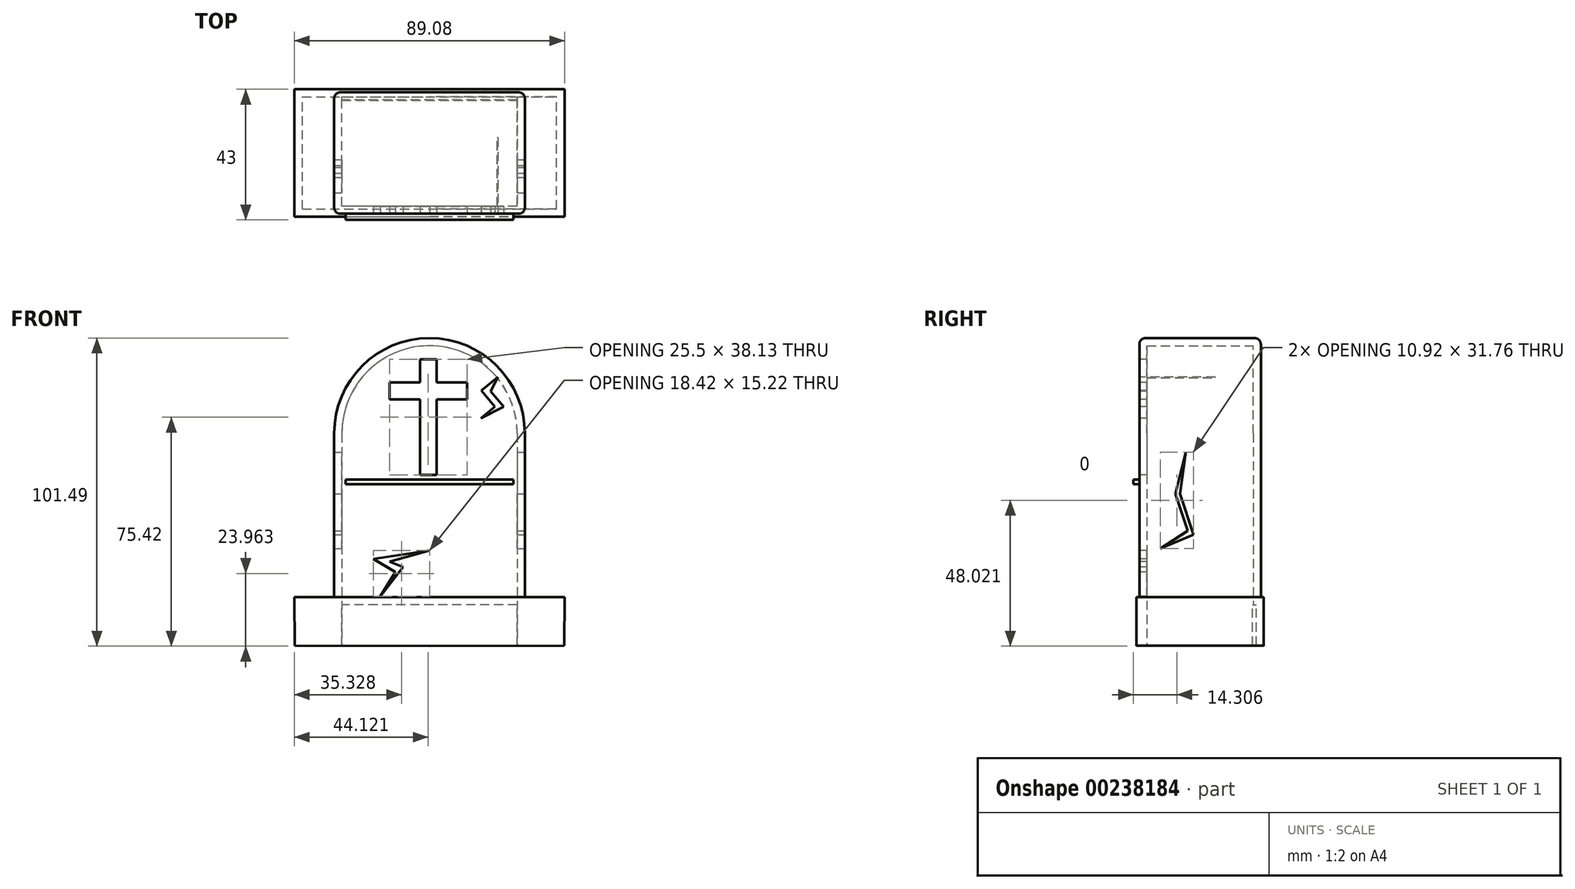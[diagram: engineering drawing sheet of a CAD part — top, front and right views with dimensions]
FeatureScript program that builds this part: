
annotation { "Feature Type Name" : "Feature", "Feature Type Description" : "" }
export const myFeature = defineFeature(function(context is Context, id is Id, definition is map)
    precondition{}
    {
        {
            var Q0;
            Q0=qCreatedBy(makeId("Front.planeOp"),FACE);
            var sketch = newSketch(context, id + "F0", { "sketchPlane" : qUnion([Q0])});
            skLineSegment(sketch, "E0", {"start": v(31.39, 27.06) * mm, "end": v(31.39, -27.25) * mm});
            skLineSegment(sketch, "E1.MirrorCS", {"start": v(-31.39, 27.06) * mm, "end": v(-31.39, -27.25) * mm});
            skArc(sketch, "E2", {"start": v(31.39, 27.06) * mm, "mid": v(0, 58.45) * mm, "end": v(-31.39, 27.06) * mm});
            skLineSegment(sketch, "E3", {"start": v(-31.39, -27.25) * mm, "end": v(31.39, -27.25) * mm});
            skSolve(sketch);
        }
        {
            var Q0;
            Q0 = qSketchRegion(id + "F0", true);
            extrude(context, id + "F1", {"entities" : qUnion([Q0]), "endBound" : BoundingType.SYMMETRIC, "depth" : 40 * mm});
        }
        {
            var Q0;
            Q0=qCreatedBy(makeId("Front.planeOp"),FACE);
            var sketch = newSketch(context, id + "F2", { "sketchPlane" : qUnion([Q0])});
            skLineSegment(sketch, "E4", {"start": v(-31.2, -26.88) * mm, "end": v(-44.54, -26.88) * mm});
            skLineSegment(sketch, "E5", {"start": v(-44.54, -26.88) * mm, "end": v(-44.4, -42.88) * mm});
            skLineSegment(sketch, "E6", {"start": v(-44.4, -42.88) * mm, "end": v(0.02, -43.04) * mm});
            skLineSegment(sketch, "E7.MirrorCS", {"start": v(44.54, -26.88) * mm, "end": v(44.4, -42.88) * mm});
            skLineSegment(sketch, "E8.MirrorCS", {"start": v(31.2, -26.88) * mm, "end": v(44.54, -26.88) * mm});
            skLineSegment(sketch, "E9.MirrorCS", {"start": v(44.4, -42.88) * mm, "end": v(-0.02, -43.04) * mm});
            skLineSegment(sketch, "E10", {"start": v(-31.2, -26.88) * mm, "end": v(31.2, -26.88) * mm});
            skSolve(sketch);
        }
        {
            var Q0;
            Q0 = qSketchRegion(id + "F2", true);
            extrude(context, id + "F3", {"entities" : qUnion([Q0]), "operationType" : NewBodyOperationType.ADD, "endBound" : BoundingType.SYMMETRIC, "depth" : 42 * mm});
        }
        {
            var Q0;
            Q0=makeQuery(id+"F3.opExtrude","SWEPT_FACE",FACE,{"disambiguationData":[OSD([sQuery(id+"F2.wireOp",EDGE,"E6")])]});
            var Q1;
            Q1=makeQuery(id+"F3.opExtrude","SWEPT_FACE",FACE,{"disambiguationData":[OSD([sQuery(id+"F2.wireOp",EDGE,"E9.MirrorCS")])]});
            shell(context, id + "F4", {"entities" : qUnion([Q0, Q1]), "thickness" : 2.5 * mm});
        }
        {
            var Q0;
            Q0=makeQuery(id+"F1.opExtrude","CAP_FACE",FACE,{"disambiguationData":[OSD([sQuery(id+"F0.wireOp",EDGE,"E0"),sQuery(id+"F0.wireOp",EDGE,"E1.MirrorCS"),sQuery(id+"F0.wireOp",EDGE,"E2"),sQuery(id+"F0.wireOp",EDGE,"E3")])],"isStart":false});
            var sketch = newSketch(context, id + "F5", { "sketchPlane" : qUnion([Q0])});
            skSolve(sketch);
        }
        {
            var Q0;
            {var subQ0=sQuery(id+"F0.wireOp",EDGE,"E2");Q0=makeQuery(id+"F5.imprint","IMPRINT",FACE,{"disambiguationData":[TD([[makeQuery(id+"F5.imprint","IMPRINT",EDGE,{"derivedFrom":makeQuery(id+"F1.opExtrude","CAP_EDGE",EDGE,{"disambiguationData":[OSD([subQ0])],"isStart":false})}),1.0]])]});}
            var sketch = newSketch(context, id + "F6", { "sketchPlane" : qUnion([Q0])});
            skLineSegment(sketch, "E11.bottom", {"start": v(-3.17, 51.45) * mm, "end": v(2.33, 51.45) * mm});
            skLineSegment(sketch, "E11.top", {"start": v(-3.17, 13.31) * mm, "end": v(2.33, 13.31) * mm});
            skLineSegment(sketch, "E11.left", {"start": v(-3.17, 51.45) * mm, "end": v(-3.17, 13.31) * mm});
            skLineSegment(sketch, "E11.right", {"start": v(2.33, 51.45) * mm, "end": v(2.33, 13.31) * mm});
            skLineSegment(sketch, "E12.bottom", {"start": v(-3.17, 43.82) * mm, "end": v(-13.17, 43.82) * mm});
            skLineSegment(sketch, "E12.top", {"start": v(-3.17, 38.32) * mm, "end": v(-13.17, 38.32) * mm});
            skLineSegment(sketch, "E12.left", {"start": v(-3.17, 43.82) * mm, "end": v(-3.17, 38.32) * mm});
            skLineSegment(sketch, "E12.right", {"start": v(-13.17, 43.82) * mm, "end": v(-13.17, 38.32) * mm});
            skLineSegment(sketch, "E13.bottom", {"start": v(2.33, 43.82) * mm, "end": v(12.33, 43.82) * mm});
            skLineSegment(sketch, "E13.top", {"start": v(2.33, 38.32) * mm, "end": v(12.33, 38.32) * mm});
            skLineSegment(sketch, "E13.left", {"start": v(2.33, 43.82) * mm, "end": v(2.33, 38.32) * mm});
            skLineSegment(sketch, "E13.right", {"start": v(12.33, 43.82) * mm, "end": v(12.33, 38.32) * mm});
            skSolve(sketch);
        }
        {
            var Q0;
            Q0 = qSketchRegion(id + "F6", true);
            extrude(context, id + "F7", {"entities" : qUnion([Q0]), "operationType" : NewBodyOperationType.REMOVE, "oppositeDirection" : true, "depth" : 25 * mm});
        }
        {
            var Q0;
            {var subQ0=sQuery(id+"F0.wireOp",EDGE,"E2");Q0=makeQuery(id+"F5.imprint","IMPRINT",FACE,{"disambiguationData":[TD([[makeQuery(id+"F5.imprint","IMPRINT",EDGE,{"derivedFrom":makeQuery(id+"F1.opExtrude","CAP_EDGE",EDGE,{"disambiguationData":[OSD([subQ0])],"isStart":false})}),1.0]])]});}
            var sketch = newSketch(context, id + "F8", { "sketchPlane" : qUnion([Q0])});
            skLineSegment(sketch, "E14.bottom", {"start": v(27.63, 11.84) * mm, "end": v(-27.63, 11.84) * mm});
            skLineSegment(sketch, "E14.top", {"start": v(27.63, 10.34) * mm, "end": v(-27.63, 10.34) * mm});
            skLineSegment(sketch, "E14.left", {"start": v(27.63, 11.84) * mm, "end": v(27.63, 10.34) * mm});
            skLineSegment(sketch, "E14.right", {"start": v(-27.63, 11.84) * mm, "end": v(-27.63, 10.34) * mm});
            skPoint(sketch, "E14.middle", {"position": v(0, 11.09) * mm});
            skSolve(sketch);
        }
        {
            var Q0;
            Q0 = qSketchRegion(id + "F8", true);
            extrude(context, id + "F9", {"entities" : qUnion([Q0]), "operationType" : NewBodyOperationType.ADD, "depth" : 2 * mm});
        }
        {
            var Q0;
            Q0=makeQuery(id+"F1.opExtrude","CAP_EDGE",EDGE,{"disambiguationData":[OSD([sQuery(id+"F0.wireOp",EDGE,"E2")])],"isStart":false});
            var Q1;
            Q1=makeQuery(id+"F1.opExtrude","CAP_EDGE",EDGE,{"disambiguationData":[OSD([sQuery(id+"F0.wireOp",EDGE,"E2")])],"isStart":true});
            fillet(context, id + "F10", {"entities" : qUnion([Q0, Q1]), "radius" : 2 * mm, "tangentPropagation" : true, "allowEdgeOverflow" : false});
        }
        {
            var Q0;
            Q0=makeQuery(id+"F1.opExtrude","SWEPT_FACE",FACE,{"disambiguationData":[OSD([sQuery(id+"F0.wireOp",EDGE,"E0")])]});
            var sketch = newSketch(context, id + "F11", { "sketchPlane" : qUnion([Q0])});
            skLineSegment(sketch, "E15", {"start": v(-13.16, -10.9) * mm, "end": v(-4.13, -5.07) * mm});
            skLineSegment(sketch, "E16", {"start": v(-4.13, -5.07) * mm, "end": v(-8.08, 7.14) * mm});
            skLineSegment(sketch, "E17", {"start": v(-8.08, 7.14) * mm, "end": v(-4.7, 20.86) * mm});
            skLineSegment(sketch, "E18", {"start": v(-4.7, 20.86) * mm, "end": v(-6.58, 7.14) * mm});
            skLineSegment(sketch, "E19", {"start": v(-6.58, 7.14) * mm, "end": v(-2.23, -6.31) * mm});
            skLineSegment(sketch, "E20", {"start": v(-2.23, -6.31) * mm, "end": v(-13.16, -10.9) * mm});
            skSolve(sketch);
        }
        {
            var Q0;
            Q0 = qSketchRegion(id + "F11", true);
            extrude(context, id + "F12", {"entities" : qUnion([Q0]), "operationType" : NewBodyOperationType.REMOVE, "oppositeDirection" : true, "depth" : 70 * mm});
        }
        {
            var Q0;
            {var subQ0=sQuery(id+"F0.wireOp",EDGE,"E2");Q0=makeQuery(id+"F5.imprint","IMPRINT",FACE,{"disambiguationData":[TD([[makeQuery(id+"F5.imprint","IMPRINT",EDGE,{"derivedFrom":makeQuery(id+"F1.opExtrude","CAP_EDGE",EDGE,{"disambiguationData":[OSD([subQ0])],"isStart":false})}),1.0]])]});}
            var sketch = newSketch(context, id + "F13", { "sketchPlane" : qUnion([Q0])});
            skLineSegment(sketch, "E21", {"start": v(-16.16, -26.69) * mm, "end": v(-11.28, -18.6) * mm});
            skLineSegment(sketch, "E22", {"start": v(-11.28, -18.6) * mm, "end": v(-18.42, -14.29) * mm});
            skLineSegment(sketch, "E23", {"start": v(-18.42, -14.29) * mm, "end": v(0, -11.46) * mm});
            skLineSegment(sketch, "E24", {"start": v(0, -11.46) * mm, "end": v(-13.16, -15.22) * mm});
            skLineSegment(sketch, "E25", {"start": v(-13.16, -15.22) * mm, "end": v(-8.65, -16.92) * mm});
            skLineSegment(sketch, "E26", {"start": v(-8.65, -16.92) * mm, "end": v(-16.16, -26.69) * mm});
            skSolve(sketch);
        }
        {
            var Q0;
            Q0 = qSketchRegion(id + "F13", true);
            extrude(context, id + "F14", {"entities" : qUnion([Q0]), "operationType" : NewBodyOperationType.REMOVE, "oppositeDirection" : true, "depth" : 25 * mm});
        }
        {
            var Q0;
            {var subQ0=sQuery(id+"F0.wireOp",EDGE,"E2");Q0=makeQuery(id+"F5.imprint","IMPRINT",FACE,{"disambiguationData":[TD([[makeQuery(id+"F5.imprint","IMPRINT",EDGE,{"derivedFrom":makeQuery(id+"F1.opExtrude","CAP_EDGE",EDGE,{"disambiguationData":[OSD([subQ0])],"isStart":false})}),1.0]])]});}
            var sketch = newSketch(context, id + "F15", { "sketchPlane" : qUnion([Q0])});
            skLineSegment(sketch, "E27", {"start": v(22.55, 45.67) * mm, "end": v(17.1, 41.16) * mm});
            skLineSegment(sketch, "E28", {"start": v(17.1, 41.16) * mm, "end": v(21.5, 35.84) * mm});
            skLineSegment(sketch, "E29", {"start": v(21.5, 35.84) * mm, "end": v(16.9, 32.03) * mm});
            skLineSegment(sketch, "E30", {"start": v(16.9, 32.03) * mm, "end": v(24.43, 35.84) * mm});
            skLineSegment(sketch, "E31", {"start": v(24.43, 35.84) * mm, "end": v(20.19, 40.97) * mm});
            skLineSegment(sketch, "E32", {"start": v(20.19, 40.97) * mm, "end": v(22.55, 45.67) * mm});
            skSolve(sketch);
        }
        {
            var Q0;
            Q0 = qSketchRegion(id + "F15", true);
            extrude(context, id + "F16", {"entities" : qUnion([Q0]), "operationType" : NewBodyOperationType.REMOVE, "oppositeDirection" : true, "depth" : 25 * mm});
        }
        {
            var Q0;
            Q0=makeQuery(id+"F4.opShell","OFFSET_FACE",FACE,{"disambiguationData":[OSD([sQuery(id+"F2.wireOp",EDGE,"E4"),sQuery(id+"F2.wireOp",EDGE,"E8.MirrorCS"),sQuery(id+"F2.wireOp",EDGE,"E10")])]});
            var sketch = newSketch(context, id + "F17", { "sketchPlane" : qUnion([Q0])});
            skPoint(sketch, "E33.oppositeSnap0", {"position": v(-28.89, 0) * mm});
            skLineSegment(sketch, "E33.bottom", {"start": v(-42.02, 18.5) * mm, "end": v(-28.89, 18.5) * mm});
            skLineSegment(sketch, "E33.top", {"start": v(-42.02, -18.5) * mm, "end": v(-28.89, -18.5) * mm});
            skLineSegment(sketch, "E33.left", {"start": v(-42.02, 18.5) * mm, "end": v(-42.02, -18.5) * mm});
            skLineSegment(sketch, "E33.right", {"start": v(-28.89, 18.5) * mm, "end": v(-28.89, -18.5) * mm});
            skSolve(sketch);
        }
        {
            var Q0;
            Q0 = qSketchRegion(id + "F17", true);
            extrude(context, id + "F18", {"entities" : qUnion([Q0]), "operationType" : NewBodyOperationType.ADD, "depth" : 13.5 * mm});
        }
        {
            var Q0;
            Q0=makeQuery(id+"F4.opShell","OFFSET_FACE",FACE,{"disambiguationData":[OSD([sQuery(id+"F2.wireOp",EDGE,"E4"),sQuery(id+"F2.wireOp",EDGE,"E8.MirrorCS"),sQuery(id+"F2.wireOp",EDGE,"E10")])]});
            var sketch = newSketch(context, id + "F19", { "sketchPlane" : qUnion([Q0])});
            skLineSegment(sketch, "E34.bottom", {"start": v(42.02, 18.5) * mm, "end": v(28.89, 18.5) * mm});
            skLineSegment(sketch, "E34.top", {"start": v(42.02, -18.5) * mm, "end": v(28.89, -18.5) * mm});
            skLineSegment(sketch, "E34.left", {"start": v(42.02, 18.5) * mm, "end": v(42.02, -18.5) * mm});
            skLineSegment(sketch, "E34.right", {"start": v(28.89, 18.5) * mm, "end": v(28.89, -18.5) * mm});
            skSolve(sketch);
        }
        {
            var Q0;
            Q0 = qSketchRegion(id + "F19", true);
            extrude(context, id + "F20", {"entities" : qUnion([Q0]), "operationType" : NewBodyOperationType.ADD, "depth" : 13.5 * mm});
        }
        {
            var Q0;
            {var subQ0=sQuery(id+"F0.wireOp",EDGE,"E1.MirrorCS");var subQ1=sQuery(id+"F0.wireOp",EDGE,"E0");var subQ2=sQuery(id+"F0.wireOp",EDGE,"E3");var subQ3=sQuery(id+"F0.wireOp",EDGE,"E2");var subQ4=sQuery(id+"F2.wireOp",EDGE,"E10");var subQ6=sQuery(id+"F2.wireOp",EDGE,"E8.MirrorCS");var subQ10=sQuery(id+"F2.wireOp",EDGE,"E4");Q0=makeQuery(id+"F20.boolean.opBoolean","SPLIT",FACE,{"disambiguationData":[TD([makeQuery(id+"F4.opShell","OFFSET_FACE",FACE,{"disambiguationData":[OSD([subQ1,subQ0,subQ3,subQ2]),TDD([makeQuery(id+"F1.opExtrude","CAP_FACE",FACE,{"disambiguationData":[OSD([subQ1,subQ0,subQ3,subQ2])],"isStart":false})])]})])],"derivedFrom":makeQuery(id+"F4.opShell","OFFSET_FACE",FACE,{"disambiguationData":[OSD([subQ10,subQ6,subQ4])]})});}
            var sketch = newSketch(context, id + "F21", { "sketchPlane" : qUnion([Q0])});
            skLineSegment(sketch, "E35.bottom", {"start": v(-28.89, 18.5) * mm, "end": v(28.89, 18.5) * mm});
            skLineSegment(sketch, "E35.top", {"start": v(-28.89, 17.5) * mm, "end": v(28.89, 17.5) * mm});
            skLineSegment(sketch, "E35.left", {"start": v(-28.89, 18.5) * mm, "end": v(-28.89, 17.5) * mm});
            skLineSegment(sketch, "E35.right", {"start": v(28.89, 18.5) * mm, "end": v(28.89, 17.5) * mm});
            skLineSegment(sketch, "E36.bottom", {"start": v(-28.85, -17.33) * mm, "end": v(28.87, -17.33) * mm});
            skLineSegment(sketch, "E36.top", {"start": v(-28.85, -18.6) * mm, "end": v(28.87, -18.6) * mm});
            skLineSegment(sketch, "E36.left", {"start": v(-28.85, -17.33) * mm, "end": v(-28.85, -18.6) * mm});
            skLineSegment(sketch, "E36.right", {"start": v(28.87, -17.33) * mm, "end": v(28.87, -18.6) * mm});
            skSolve(sketch);
        }
        {
            var Q0;
            Q0 = qSketchRegion(id + "F21", true);
            extrude(context, id + "F22", {"entities" : qUnion([Q0]), "operationType" : NewBodyOperationType.ADD, "depth" : 13.5 * mm});
        }
    });
